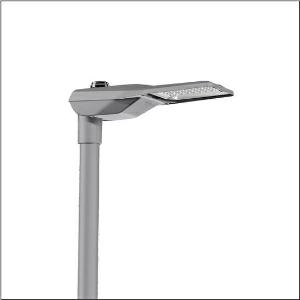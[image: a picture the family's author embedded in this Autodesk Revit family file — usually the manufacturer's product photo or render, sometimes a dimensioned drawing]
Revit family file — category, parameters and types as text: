
# Revit family: streetlight_sl_21_mini___st1_0a_5xe6d57n08jb_a4a3
name_source: partatom
category: Lighting Fixtures
units: mm (PartAtom-declared; Revit-internal decimal feet)

## family parameters
Cut with Voids When Loaded = No
Host = Face
Light Source = No
Part Type = Normal
Room Calculation Point = No
Round Connector Dimension = Use Diameter
Shared = No

## types (1)
- --- (1 x LED, 11030 lm, 87.3 W, 3000K)
    Apparent Load = 87 VA
    CIE Flux Codes = 40 73 97 100 100
    Color Rendering = 80
    Color Temperature = 3000K
    Default Elevation = 1800 mm
    Description = Streetlight SL 21 mini, mast luminaire, primary light control with lens, of PMMA, primary optical cover: cover, of toughened safety glass, transparent, light distribution: ST1.0a, light emission: direct distribution, primary light characteristic: asymmetric, installation type: side-entry, LED, 3G 2.5mm², High Power LED, rated luminous flux: 11.030lm, luminous efficacy: 126lm/W, light colour: 830, colour temperature: 3000K, control gear: NEMA (7pin), control: overheat protection, pre-setting: linear dimming characteristic, constant luminous flux control, time-dependent luminous flux control, flexible luminous flux parameterisation, mains connection: 230..240V, AC, 50/60Hz, connection cable pre-assembled, cable length: 10,5m, wiring characteristics: H05VV-F, start of lifetime: 87W, end of service life: 90W, reduction: 40W, luminaire housing, of diecast aluminium (EN AC-44300), powder-coated, SITECO metallic grey (DB 702S), corrosivity category C5 high according to DIN EN ISO 12944, multi-level sealing system, sealing non-destructively replaceable, inclination adjustable: 0°, 5°, 10°, 15°, length: 628mm, width: 235mm, height: 110mm, spigot size: 42mm (side-entry), mounting height: 4..8m, protection rating (complete): IP66, insulation class (complete): insulation class I (protective earthing), certification: CE, ENEC, ENEC+, VDE, impact resistance: IK10, permissible operating ambient temperature for outdoor applications: -40..+50°C, standard-compliant lighting for roads and squares, packaging unit: 1 piece

Light Distribution: ST1.0a
    Height = 110 mm
    Lamp = 1 x LED
    Lamp Light Flux = 11030 lm
    Lamp Power = 87.3 W
    Lamp count = 1
    Length = 625 mm
    Luminous efficacy = 126 lm/W
    Manufacturer = Siteco
    ModVariant = No
    Model = 5XE6D57N08JB
    Mounting Place = Pole
    Mounting Type = Pole top
    Number of Poles = 1
    OnlyDefault = Yes
    Power Factor = 1
    Product Name = Streetlight SL 21 mini | ST1.0a
    Product group = mast luminaire | pylon top
    ProductGroupID = 6100
    Protection Class = Protection class I
    Protection Degree = IP 66
    RLX_Detail_Level = 1
    RLX_Emergency_Light_Flux = 0 lm
    RLX_Emergency_Type = 0
    RLX_Emergency_Type_DB = No
    RlxData = <blob elided: 25993 chars, md5=fd914975>
    Socket = socket
    Standby Power = 0 W
    System Light Flux = 11030 lm
    System Power = 87 W
    Type Comments = factory setting: luminous flux: 100 % | dim-lin: 254 | 915 mA
    Type Image = l_1294379.jpg
    URL = http://relux.com
    VarID = @adj_136333
    Voltage = 0 V
    Weight = 0.00 kg
    Width = 234 mm

## geometry (parser evidence)
native form markers: Blend x4, Sweep x12
no freeform markers — native parametric forms only
